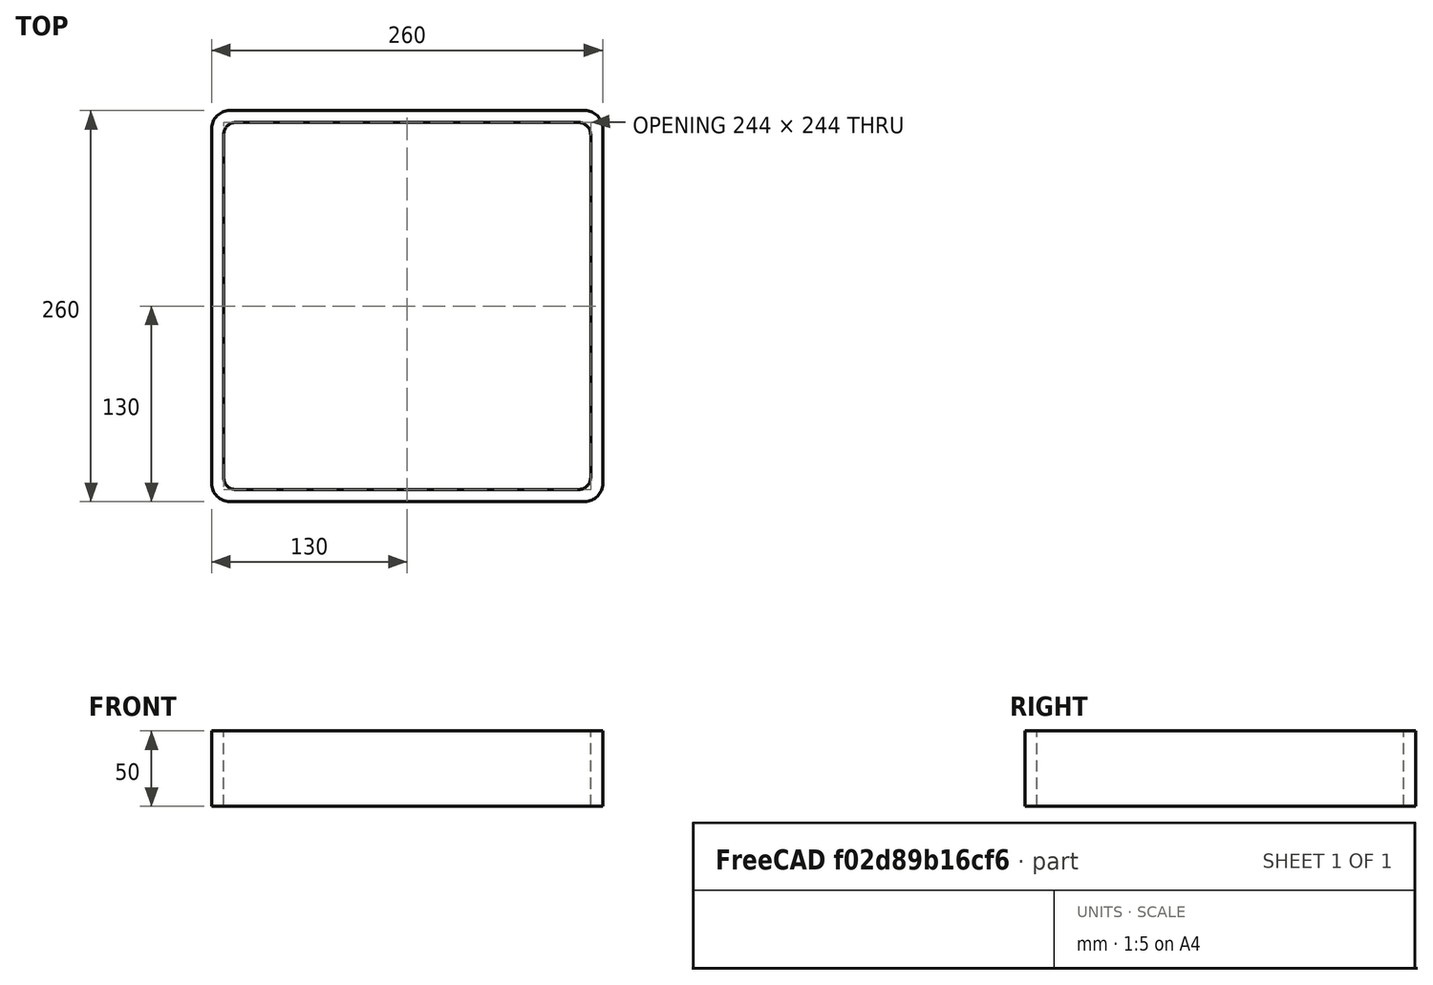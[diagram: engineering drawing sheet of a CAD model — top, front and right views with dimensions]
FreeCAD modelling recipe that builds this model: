
FCSTD DOCUMENT  (FreeCAD 0.15R4671 (Git))
Label: Square hollow section 260x260x8 EN10219 S235JRH
License: All rights reserved
LicenseURL: http://en.wikipedia.org/wiki/All_rights_reserved
objects: Sketcher::SketchObject×1, Part::Extrusion×1
note: 2 computed .brp shape members not serialized (recipe doc carries the construction recipe); baked Part::Feature solids carry a one-line shape summary decoded from their .brp

FEATURE [Sketcher::SketchObject] Sketch
  sketch-geometry (16):
    g0: LineSegment StartX=-114 StartY=122 StartZ=0 EndX=114 EndY=122 EndZ=0
    g1: LineSegment StartX=122 StartY=114 StartZ=0 EndX=122 EndY=-114 EndZ=0
    g2: LineSegment StartX=114 StartY=-122 StartZ=0 EndX=-114 EndY=-122 EndZ=0
    g3: LineSegment StartX=-122 StartY=-114 StartZ=0 EndX=-122 EndY=114 EndZ=0
    g4: LineSegment StartX=-118 StartY=130 StartZ=0 EndX=118 EndY=130 EndZ=0
    g5: LineSegment StartX=130 StartY=118 StartZ=0 EndX=130 EndY=-118 EndZ=0
    g6: LineSegment StartX=118 StartY=-130 StartZ=0 EndX=-118 EndY=-130 EndZ=0
    g7: LineSegment StartX=-130 StartY=-118 StartZ=0 EndX=-130 EndY=118 EndZ=0
    g8: ArcOfCircle CenterX=-114 CenterY=114 CenterZ=0 NormalX=0 NormalY=0 NormalZ=1 Radius=8 StartAngle=1.5708 EndAngle=3.14159
    g9: ArcOfCircle CenterX=114 CenterY=114 CenterZ=0 NormalX=0 NormalY=0 NormalZ=1 Radius=8 StartAngle=0 EndAngle=1.5708
    g10: ArcOfCircle CenterX=114 CenterY=-114 CenterZ=0 NormalX=0 NormalY=0 NormalZ=1 Radius=8 StartAngle=4.71239 EndAngle=6.28319
    g11: ArcOfCircle CenterX=-114 CenterY=-114 CenterZ=0 NormalX=0 NormalY=0 NormalZ=1 Radius=8 StartAngle=3.14159 EndAngle=4.71239
    g12: ArcOfCircle CenterX=118 CenterY=118 CenterZ=0 NormalX=0 NormalY=0 NormalZ=1 Radius=12 StartAngle=0 EndAngle=1.5708
    g13: ArcOfCircle CenterX=118 CenterY=-118 CenterZ=0 NormalX=0 NormalY=0 NormalZ=1 Radius=12 StartAngle=4.71239 EndAngle=6.28319
    g14: ArcOfCircle CenterX=-118 CenterY=-118 CenterZ=0 NormalX=0 NormalY=0 NormalZ=1 Radius=12 StartAngle=3.14159 EndAngle=4.71239
    g15: ArcOfCircle CenterX=-118 CenterY=118 CenterZ=0 NormalX=0 NormalY=0 NormalZ=1 Radius=12 StartAngle=1.5708 EndAngle=3.14159
  constraints (36):
    c: Horizontal(g2)
    c: Vertical(g3)
    c: Horizontal(g6)
    c: Vertical(g7)
    c: Tangent(g3,g8) = 1.5708
    c: Tangent(g0,g8) = 1.5708
    c: Tangent(g0,g9) = 1.5708
    c: Tangent(g1,g9) = 1.5708
    c: Tangent(g1,g10) = 1.5708
    c: Tangent(g2,g10) = 1.5708
    c: Tangent(g2,g11) = 1.5708
    c: Tangent(g3,g11) = 1.5708
    c: Tangent(g4,g12) = 1.5708
    c: Tangent(g5,g12) = 1.5708
    c: Tangent(g5,g13) = 1.5708
    c: Tangent(g6,g13) = 1.5708
    c: Tangent(g6,g14) = 1.5708
    c: Tangent(g7,g14) = 1.5708
    c: Tangent(g7,g15) = 1.5708
    c: Tangent(g4,g15) = 1.5708
    c: Equal(g9,g8)
    c: Equal(g9,g11)
    c: Equal(g9,g10)
    c: Equal(g12,g15)
    c: Equal(g12,g14)
    c: Equal(g12,g13)
    c: Symmetric(g4,g6,g-1)
    c: Symmetric(g7,g5,g-2)
    c: DistanceY(g4,g6) = -260
    c: DistanceX(g7,g5) = 260
    c: Symmetric(g3,g1,g-2)
    c: Symmetric(g0,g2,g-1)
    c: DistanceY(g0,g4) = 8
    c: DistanceX(g5,g1) = -8
    c: Radius(g9) = 8
    c: Radius(g12) = 12
FEATURE [Part::Extrusion] Extrude  label="Square hollow section 260x260x8 EN10219 S235JRH"
  Base = -> Sketch
  Dir = (0,0,50)
  Solid = true
